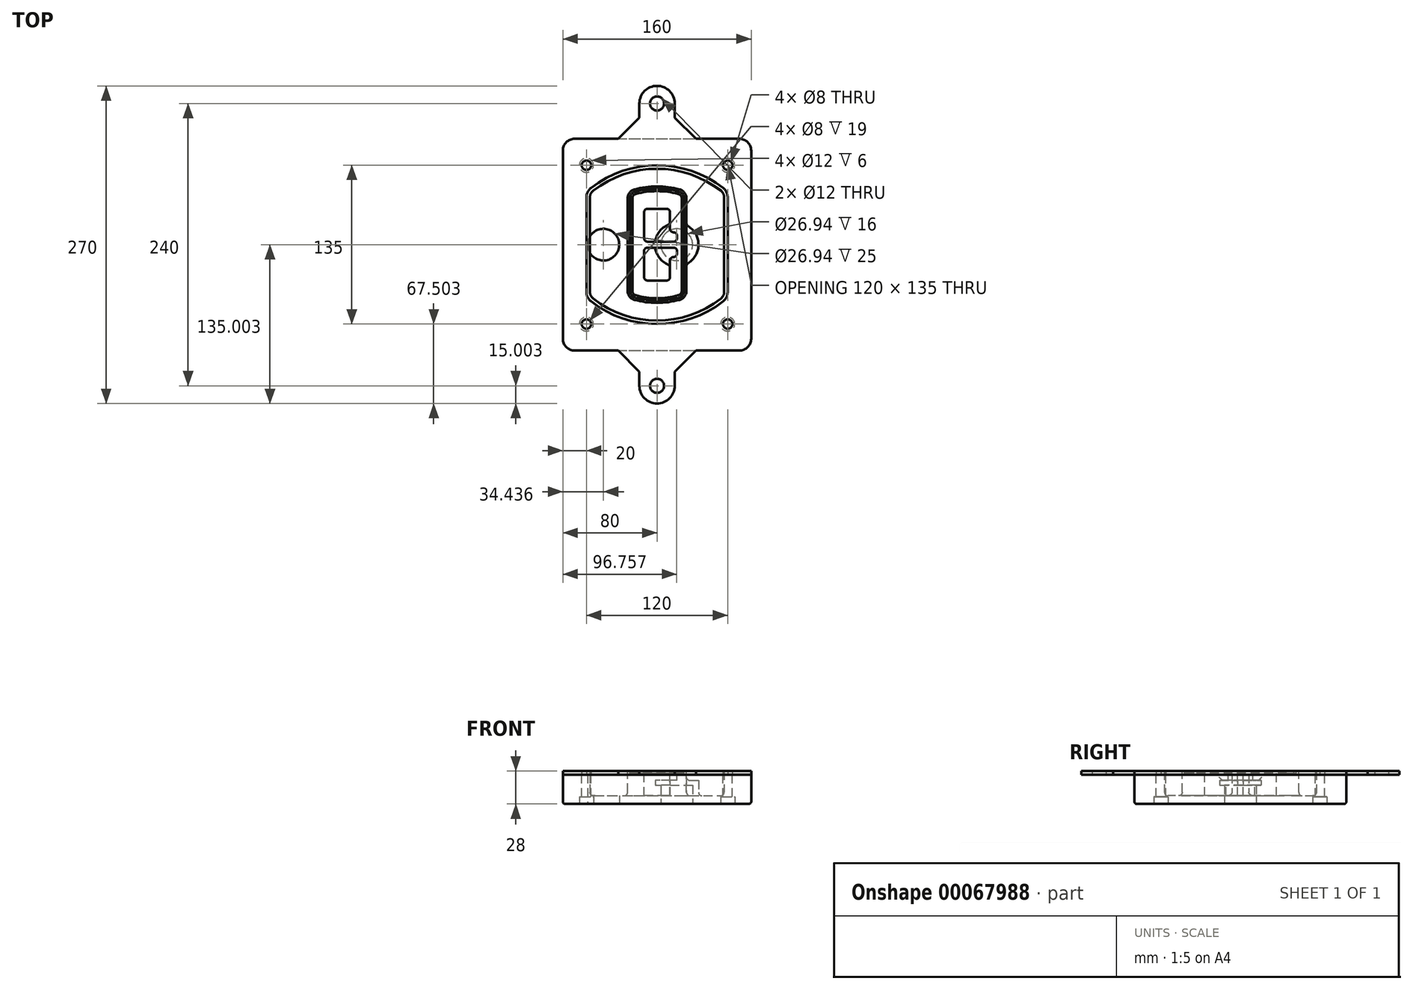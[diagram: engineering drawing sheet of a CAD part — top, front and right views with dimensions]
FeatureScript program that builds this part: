
annotation { "Feature Type Name" : "Feature", "Feature Type Description" : "" }
export const myFeature = defineFeature(function(context is Context, id is Id, definition is map)
    precondition{}
    {
        {
            var Q0;
            Q0=qCreatedBy(makeId("Top.planeOp"),FACE);
            var sketch = newSketch(context, id + "F0", { "sketchPlane" : qUnion([Q0])});
            skPoint(sketch, "E0.rect.middle", {"position": v(0, 0) * mm});
            skLineSegment(sketch, "E1.bottom", {"start": v(24.05, 28.38) * mm, "end": v(164.05, 28.38) * mm});
            skLineSegment(sketch, "E1.top", {"start": v(24.05, 208.38) * mm, "end": v(164.05, 208.38) * mm});
            skLineSegment(sketch, "E1.left", {"start": v(14.05, 38.38) * mm, "end": v(14.05, 198.38) * mm});
            skLineSegment(sketch, "E1.right", {"start": v(174.05, 38.38) * mm, "end": v(174.05, 198.38) * mm});
            skLineSegment(sketch, "E2", {"start": v(14.05, 208.38) * mm, "end": v(174.05, 28.38) * mm, "construction": true});
            skLineSegment(sketch, "E3", {"start": v(174.05, 208.38) * mm, "end": v(14.05, 28.38) * mm, "construction": true});
            skCircle(sketch, "E4", {"center": v(34.05, 185.88) * mm, "radius": 4 * mm});
            skCircle(sketch, "E5", {"center": v(154.05, 185.88) * mm, "radius": 4 * mm});
            skCircle(sketch, "E6", {"center": v(154.05, 50.88) * mm, "radius": 4 * mm});
            skCircle(sketch, "E7", {"center": v(34.05, 50.88) * mm, "radius": 4 * mm});
            skLineSegment(sketch, "E8", {"start": v(34.05, 185.88) * mm, "end": v(154.05, 185.88) * mm, "construction": true});
            skLineSegment(sketch, "E9", {"start": v(154.05, 185.88) * mm, "end": v(154.05, 50.88) * mm, "construction": true});
            skLineSegment(sketch, "E10", {"start": v(154.05, 50.88) * mm, "end": v(34.05, 50.88) * mm, "construction": true});
            skLineSegment(sketch, "E11", {"start": v(34.05, 50.88) * mm, "end": v(34.05, 185.88) * mm, "construction": true});
            skLineSegment(sketch, "E12", {"start": v(34.05, 158.68) * mm, "end": v(34.05, 78.09) * mm});
            skLineSegment(sketch, "E13", {"start": v(154.05, 158.68) * mm, "end": v(154.05, 78.09) * mm});
            skArc(sketch, "E14", {"start": v(150.2, 166.56) * mm, "mid": v(94.05, 185.88) * mm, "end": v(37.9, 166.56) * mm});
            skArc(sketch, "E15", {"start": v(37.9, 70.2) * mm, "mid": v(94.05, 50.88) * mm, "end": v(150.2, 70.2) * mm});
            skLineSegment(sketch, "E16", {"start": v(34.05, 118.38) * mm, "end": v(154.05, 118.38) * mm, "construction": true});
            skPoint(sketch, "E17.visualSharp", {"position": v(34.05, 73.38) * mm});
            skArc(sketch, "E17.filletArc", {"start": v(34.05, 78.09) * mm, "mid": v(35.06, 73.7) * mm, "end": v(37.9, 70.2) * mm});
            skPoint(sketch, "E18.visualSharp", {"position": v(34.05, 163.38) * mm});
            skArc(sketch, "E18.filletArc", {"start": v(37.9, 166.56) * mm, "mid": v(35.06, 163.06) * mm, "end": v(34.05, 158.68) * mm});
            skPoint(sketch, "E19.visualSharp", {"position": v(154.05, 163.38) * mm});
            skArc(sketch, "E19.filletArc", {"start": v(154.05, 158.68) * mm, "mid": v(153.04, 163.06) * mm, "end": v(150.2, 166.56) * mm});
            skPoint(sketch, "E20.visualSharp", {"position": v(154.05, 73.38) * mm});
            skArc(sketch, "E20.filletArc", {"start": v(150.2, 70.2) * mm, "mid": v(153.04, 73.7) * mm, "end": v(154.05, 78.09) * mm});
            skPoint(sketch, "E21.visualSharp", {"position": v(14.05, 208.38) * mm});
            skArc(sketch, "E21.filletArc", {"start": v(24.05, 208.38) * mm, "mid": v(16.98, 205.45) * mm, "end": v(14.05, 198.38) * mm});
            skPoint(sketch, "E22.visualSharp", {"position": v(174.05, 208.38) * mm});
            skArc(sketch, "E22.filletArc", {"start": v(174.05, 198.38) * mm, "mid": v(171.12, 205.45) * mm, "end": v(164.05, 208.38) * mm});
            skPoint(sketch, "E23.visualSharp", {"position": v(174.05, 28.38) * mm});
            skArc(sketch, "E23.filletArc", {"start": v(164.05, 28.38) * mm, "mid": v(171.12, 31.31) * mm, "end": v(174.05, 38.38) * mm});
            skPoint(sketch, "E24.visualSharp", {"position": v(14.05, 28.38) * mm});
            skArc(sketch, "E24.filletArc", {"start": v(14.05, 38.38) * mm, "mid": v(16.98, 31.31) * mm, "end": v(24.05, 28.38) * mm});
            skArc(sketch, "E25.0", {"start": v(151.05, 158.68) * mm, "mid": v(150.34, 161.75) * mm, "end": v(148.36, 164.2) * mm});
            skLineSegment(sketch, "E25.1", {"start": v(151.05, 158.68) * mm, "end": v(151.05, 78.09) * mm});
            skArc(sketch, "E25.2", {"start": v(148.36, 72.57) * mm, "mid": v(150.34, 75.02) * mm, "end": v(151.05, 78.09) * mm});
            skArc(sketch, "E25.3", {"start": v(39.74, 72.57) * mm, "mid": v(94.05, 53.88) * mm, "end": v(148.36, 72.57) * mm});
            skArc(sketch, "E25.4", {"start": v(37.05, 78.09) * mm, "mid": v(37.76, 75.02) * mm, "end": v(39.74, 72.57) * mm});
            skArc(sketch, "E25.5", {"start": v(148.36, 164.2) * mm, "mid": v(94.05, 182.88) * mm, "end": v(39.74, 164.2) * mm});
            skLineSegment(sketch, "E25.6", {"start": v(37.05, 158.68) * mm, "end": v(37.05, 78.09) * mm});
            skArc(sketch, "E25.7", {"start": v(39.74, 164.2) * mm, "mid": v(37.76, 161.75) * mm, "end": v(37.05, 158.68) * mm});
            skArc(sketch, "E26.0", {"start": v(35.43, 169.71) * mm, "mid": v(31.47, 164.82) * mm, "end": v(30.05, 158.68) * mm});
            skArc(sketch, "E26.1", {"start": v(152.67, 169.71) * mm, "mid": v(94.05, 189.88) * mm, "end": v(35.43, 169.71) * mm});
            skArc(sketch, "E26.2", {"start": v(158.05, 158.68) * mm, "mid": v(156.63, 164.82) * mm, "end": v(152.67, 169.71) * mm});
            skLineSegment(sketch, "E26.3", {"start": v(158.05, 158.68) * mm, "end": v(158.05, 78.09) * mm});
            skArc(sketch, "E26.4", {"start": v(152.67, 67.05) * mm, "mid": v(156.63, 71.95) * mm, "end": v(158.05, 78.09) * mm});
            skLineSegment(sketch, "E26.5", {"start": v(30.05, 158.68) * mm, "end": v(30.05, 78.09) * mm});
            skArc(sketch, "E26.6", {"start": v(35.43, 67.05) * mm, "mid": v(94.05, 46.88) * mm, "end": v(152.67, 67.05) * mm});
            skArc(sketch, "E26.7", {"start": v(30.05, 78.09) * mm, "mid": v(31.47, 71.95) * mm, "end": v(35.43, 67.05) * mm});
            skSolve(sketch);
        }
        {
            var Q0;
            Q0=makeQuery(id+"F0.imprint","IMPRINT",FACE,{"disambiguationData":[TD([[makeQuery(id+"F0.imprint","IMPRINT",EDGE,{"derivedFrom":sQuery(id+"F0.wireOp",EDGE,"E1.bottom")}),1.0]])]});
            var Q1;
            Q1=makeQuery(id+"F0.imprint","IMPRINT",FACE,{"disambiguationData":[TD([[makeQuery(id+"F0.imprint","IMPRINT",EDGE,{"derivedFrom":sQuery(id+"F0.wireOp",EDGE,"E12")}),1.0]])]});
            var Q2;
            Q2=makeQuery(id+"F0.imprint","IMPRINT",FACE,{"disambiguationData":[TD([[makeQuery(id+"F0.imprint","IMPRINT",EDGE,{"derivedFrom":sQuery(id+"F0.wireOp",EDGE,"E25.0")}),1.0]])]});
            var Q3;
            Q3=makeQuery(id+"F0.imprint","IMPRINT",FACE,{"disambiguationData":[TD([[makeQuery(id+"F0.imprint","IMPRINT",EDGE,{"derivedFrom":sQuery(id+"F0.wireOp",EDGE,"E12")}),-1.0]])]});
            extrude(context, id + "F1", {"entities" : qUnion([Q0, Q1, Q2, Q3]), "oppositeDirection" : true, "depth" : 25 * mm});
        }
        {
            var Q0;
            Q0=makeQuery(id+"F0.imprint","IMPRINT",FACE,{"disambiguationData":[TD([[makeQuery(id+"F0.imprint","IMPRINT",EDGE,{"derivedFrom":sQuery(id+"F0.wireOp",EDGE,"E12")}),1.0]])]});
            extrude(context, id + "F2", {"entities" : qUnion([Q0]), "operationType" : NewBodyOperationType.ADD, "depth" : 3 * mm});
        }
        {
            var Q0;
            Q0=makeQuery(id+"F0.imprint","IMPRINT",FACE,{"disambiguationData":[TD([[makeQuery(id+"F0.imprint","IMPRINT",EDGE,{"derivedFrom":sQuery(id+"F0.wireOp",EDGE,"E25.0")}),1.0]])]});
            extrude(context, id + "F3", {"entities" : qUnion([Q0]), "operationType" : NewBodyOperationType.REMOVE, "oppositeDirection" : true, "depth" : 18 * mm});
        }
        {
            var Q0;
            Q0=makeQuery(id+"F2.opExtrude","CAP_FACE",FACE,{"disambiguationData":[OSD([sQuery(id+"F0.wireOp",EDGE,"E12"),sQuery(id+"F0.wireOp",EDGE,"E13"),sQuery(id+"F0.wireOp",EDGE,"E14"),sQuery(id+"F0.wireOp",EDGE,"E15"),sQuery(id+"F0.wireOp",EDGE,"E17.filletArc"),sQuery(id+"F0.wireOp",EDGE,"E18.filletArc"),sQuery(id+"F0.wireOp",EDGE,"E19.filletArc"),sQuery(id+"F0.wireOp",EDGE,"E20.filletArc"),sQuery(id+"F0.wireOp",EDGE,"E25.0"),sQuery(id+"F0.wireOp",EDGE,"E25.1"),sQuery(id+"F0.wireOp",EDGE,"E25.2"),sQuery(id+"F0.wireOp",EDGE,"E25.3"),sQuery(id+"F0.wireOp",EDGE,"E25.4"),sQuery(id+"F0.wireOp",EDGE,"E25.5"),sQuery(id+"F0.wireOp",EDGE,"E25.6"),sQuery(id+"F0.wireOp",EDGE,"E25.7")])],"isStart":false});
            var sketch = newSketch(context, id + "F4", { "sketchPlane" : qUnion([Q0])});
            skArc(sketch, "E27.0", {"start": v(74.97, 71.41) * mm, "mid": v(94.05, 68.88) * mm, "end": v(113.13, 71.41) * mm});
            skArc(sketch, "E28.0", {"start": v(113.13, 165.35) * mm, "mid": v(94.05, 167.88) * mm, "end": v(74.97, 165.35) * mm});
            skLineSegment(sketch, "E29", {"start": v(69.05, 157.63) * mm, "end": v(69.05, 79.14) * mm});
            skLineSegment(sketch, "E30", {"start": v(119.05, 157.63) * mm, "end": v(119.05, 79.14) * mm});
            skLineSegment(sketch, "E31", {"start": v(69.05, 163.48) * mm, "end": v(119.05, 163.48) * mm, "construction": true});
            skLineSegment(sketch, "E32", {"start": v(69.05, 73.28) * mm, "end": v(119.05, 73.28) * mm, "construction": true});
            skPoint(sketch, "E33.visualSharp", {"position": v(69.05, 163.48) * mm});
            skArc(sketch, "E33.filletArc", {"start": v(74.97, 165.35) * mm, "mid": v(70.7, 162.5) * mm, "end": v(69.05, 157.63) * mm});
            skPoint(sketch, "E34.visualSharp", {"position": v(119.05, 163.48) * mm});
            skArc(sketch, "E34.filletArc", {"start": v(119.05, 157.63) * mm, "mid": v(117.4, 162.5) * mm, "end": v(113.13, 165.35) * mm});
            skPoint(sketch, "E35.visualSharp", {"position": v(119.05, 73.28) * mm});
            skArc(sketch, "E35.filletArc", {"start": v(113.13, 71.41) * mm, "mid": v(117.4, 74.27) * mm, "end": v(119.05, 79.14) * mm});
            skPoint(sketch, "E36.visualSharp", {"position": v(69.05, 73.28) * mm});
            skArc(sketch, "E36.filletArc", {"start": v(69.05, 79.14) * mm, "mid": v(70.7, 74.27) * mm, "end": v(74.97, 71.41) * mm});
            skArc(sketch, "E37.0", {"start": v(148.36, 164.2) * mm, "mid": v(94.05, 182.88) * mm, "end": v(39.74, 164.2) * mm});
            skArc(sketch, "E37.1", {"start": v(39.74, 164.2) * mm, "mid": v(37.76, 161.75) * mm, "end": v(37.05, 158.68) * mm});
            skLineSegment(sketch, "E37.2", {"start": v(37.05, 158.68) * mm, "end": v(37.05, 78.09) * mm});
            skArc(sketch, "E37.3", {"start": v(37.05, 78.09) * mm, "mid": v(37.76, 75.02) * mm, "end": v(39.74, 72.57) * mm});
            skArc(sketch, "E37.4", {"start": v(39.74, 72.57) * mm, "mid": v(94.05, 53.88) * mm, "end": v(148.36, 72.57) * mm});
            skArc(sketch, "E37.5", {"start": v(148.36, 72.57) * mm, "mid": v(150.34, 75.02) * mm, "end": v(151.05, 78.09) * mm});
            skLineSegment(sketch, "E37.6", {"start": v(151.05, 158.68) * mm, "end": v(151.05, 78.09) * mm});
            skArc(sketch, "E37.7", {"start": v(151.05, 158.68) * mm, "mid": v(150.34, 161.75) * mm, "end": v(148.36, 164.2) * mm});
            skLineSegment(sketch, "E38.0", {"start": v(117.05, 157.63) * mm, "end": v(117.05, 79.14) * mm});
            skArc(sketch, "E38.1", {"start": v(112.61, 73.34) * mm, "mid": v(115.81, 75.49) * mm, "end": v(117.05, 79.14) * mm});
            skArc(sketch, "E38.2", {"start": v(75.49, 73.34) * mm, "mid": v(94.05, 70.88) * mm, "end": v(112.61, 73.34) * mm});
            skArc(sketch, "E38.3", {"start": v(71.05, 79.14) * mm, "mid": v(72.29, 75.49) * mm, "end": v(75.49, 73.34) * mm});
            skLineSegment(sketch, "E38.4", {"start": v(71.05, 157.63) * mm, "end": v(71.05, 79.14) * mm});
            skArc(sketch, "E38.5", {"start": v(117.05, 157.63) * mm, "mid": v(115.81, 161.28) * mm, "end": v(112.61, 163.42) * mm});
            skArc(sketch, "E38.6", {"start": v(75.49, 163.42) * mm, "mid": v(72.29, 161.28) * mm, "end": v(71.05, 157.63) * mm});
            skArc(sketch, "E38.7", {"start": v(112.61, 163.42) * mm, "mid": v(94.05, 165.88) * mm, "end": v(75.49, 163.42) * mm});
            skArc(sketch, "E39.0", {"start": v(115.05, 157.63) * mm, "mid": v(114.23, 160.06) * mm, "end": v(112.1, 161.5) * mm});
            skLineSegment(sketch, "E39.1", {"start": v(115.05, 157.63) * mm, "end": v(115.05, 79.14) * mm});
            skArc(sketch, "E39.2", {"start": v(112.1, 75.27) * mm, "mid": v(114.23, 76.7) * mm, "end": v(115.05, 79.14) * mm});
            skArc(sketch, "E39.3", {"start": v(76, 75.27) * mm, "mid": v(94.05, 72.88) * mm, "end": v(112.1, 75.27) * mm});
            skArc(sketch, "E39.4", {"start": v(73.05, 79.14) * mm, "mid": v(73.87, 76.7) * mm, "end": v(76, 75.27) * mm});
            skArc(sketch, "E39.5", {"start": v(112.1, 161.5) * mm, "mid": v(94.05, 163.88) * mm, "end": v(76, 161.5) * mm});
            skLineSegment(sketch, "E39.6", {"start": v(73.05, 157.63) * mm, "end": v(73.05, 79.14) * mm});
            skArc(sketch, "E39.7", {"start": v(76, 161.5) * mm, "mid": v(73.87, 160.06) * mm, "end": v(73.05, 157.63) * mm});
            skLineSegment(sketch, "E40", {"start": v(69.05, 118.38) * mm, "end": v(119.05, 118.38) * mm, "construction": true});
            skLineSegment(sketch, "E41", {"start": v(83.05, 123.88) * mm, "end": v(83.05, 145.88) * mm});
            skLineSegment(sketch, "E42", {"start": v(86.05, 148.88) * mm, "end": v(102.05, 148.88) * mm});
            skLineSegment(sketch, "E43", {"start": v(105.05, 145.88) * mm, "end": v(105.05, 131.88) * mm});
            skLineSegment(sketch, "E44", {"start": v(108.05, 128.88) * mm, "end": v(108.05, 128.88) * mm});
            skLineSegment(sketch, "E45", {"start": v(111.05, 125.88) * mm, "end": v(111.05, 123.88) * mm});
            skLineSegment(sketch, "E46", {"start": v(108.05, 120.88) * mm, "end": v(86.05, 120.88) * mm});
            skPoint(sketch, "E47.visualSharp", {"position": v(83.05, 148.88) * mm});
            skArc(sketch, "E47.filletArc", {"start": v(86.05, 148.88) * mm, "mid": v(83.93, 148) * mm, "end": v(83.05, 145.88) * mm});
            skPoint(sketch, "E48.visualSharp", {"position": v(105.05, 148.88) * mm});
            skArc(sketch, "E48.filletArc", {"start": v(105.05, 145.88) * mm, "mid": v(104.17, 148) * mm, "end": v(102.05, 148.88) * mm});
            skPoint(sketch, "E49.visualSharp", {"position": v(105.05, 128.88) * mm});
            skArc(sketch, "E49.filletArc", {"start": v(105.05, 131.88) * mm, "mid": v(105.93, 129.76) * mm, "end": v(108.05, 128.88) * mm});
            skPoint(sketch, "E50.visualSharp", {"position": v(111.05, 128.88) * mm});
            skArc(sketch, "E50.filletArc", {"start": v(111.05, 125.88) * mm, "mid": v(110.17, 128) * mm, "end": v(108.05, 128.88) * mm});
            skPoint(sketch, "E51.visualSharp", {"position": v(111.05, 120.88) * mm});
            skArc(sketch, "E51.filletArc", {"start": v(108.05, 120.88) * mm, "mid": v(110.17, 121.76) * mm, "end": v(111.05, 123.88) * mm});
            skPoint(sketch, "E52.visualSharp", {"position": v(83.05, 120.88) * mm});
            skArc(sketch, "E52.filletArc", {"start": v(83.05, 123.88) * mm, "mid": v(83.93, 121.76) * mm, "end": v(86.05, 120.88) * mm});
            skLineSegment(sketch, "E53.0.MirrorCS", {"start": v(108.05, 115.88) * mm, "end": v(86.05, 115.88) * mm});
            skArc(sketch, "E54.0.MirrorCS", {"start": v(83.05, 112.88) * mm, "mid": v(83.93, 115) * mm, "end": v(86.05, 115.88) * mm});
            skLineSegment(sketch, "E55.0.MirrorCS", {"start": v(83.05, 112.88) * mm, "end": v(83.05, 90.88) * mm});
            skArc(sketch, "E56.0.MirrorCS", {"start": v(86.05, 87.88) * mm, "mid": v(83.93, 88.76) * mm, "end": v(83.05, 90.88) * mm});
            skLineSegment(sketch, "E57.0.MirrorCS", {"start": v(86.05, 87.88) * mm, "end": v(102.05, 87.88) * mm});
            skArc(sketch, "E58.0.MirrorCS", {"start": v(105.05, 90.88) * mm, "mid": v(104.17, 88.76) * mm, "end": v(102.05, 87.88) * mm});
            skLineSegment(sketch, "E59.0.MirrorCS", {"start": v(105.05, 90.88) * mm, "end": v(105.05, 104.88) * mm});
            skArc(sketch, "E60.0.MirrorCS", {"start": v(105.05, 104.88) * mm, "mid": v(105.93, 107) * mm, "end": v(108.05, 107.88) * mm});
            skArc(sketch, "E61.0.MirrorCS", {"start": v(111.05, 110.88) * mm, "mid": v(110.17, 108.76) * mm, "end": v(108.05, 107.88) * mm});
            skLineSegment(sketch, "E62.0.MirrorCS", {"start": v(111.05, 110.88) * mm, "end": v(111.05, 112.88) * mm});
            skArc(sketch, "E63.0.MirrorCS", {"start": v(108.05, 115.88) * mm, "mid": v(110.17, 115) * mm, "end": v(111.05, 112.88) * mm});
            skSolve(sketch);
        }
        {
            var Q0;
            Q0=makeQuery(id+"F4.imprint","IMPRINT",FACE,{"disambiguationData":[TD([[makeQuery(id+"F4.imprint","IMPRINT",EDGE,{"derivedFrom":sQuery(id+"F4.wireOp",EDGE,"E27.0")}),1.0]])]});
            var Q1;
            Q1=makeQuery(id+"F4.imprint","IMPRINT",FACE,{"disambiguationData":[TD([[makeQuery(id+"F4.imprint","IMPRINT",EDGE,{"derivedFrom":sQuery(id+"F4.wireOp",EDGE,"E38.0")}),-1.0]])]});
            var Q2;
            Q2=makeQuery(id+"F4.imprint","IMPRINT",FACE,{"disambiguationData":[TD([[makeQuery(id+"F4.imprint","IMPRINT",EDGE,{"derivedFrom":sQuery(id+"F4.wireOp",EDGE,"E39.0")}),1.0]])]});
            extrude(context, id + "F5", {"entities" : qUnion([Q0, Q1, Q2]), "operationType" : NewBodyOperationType.ADD, "endBound" : BoundingType.UP_TO_NEXT, "oppositeDirection" : true, "depth" : 25 * mm});
        }
        {
            var Q0;
            Q0=makeQuery(id+"F4.imprint","IMPRINT",FACE,{"disambiguationData":[TD([[makeQuery(id+"F4.imprint","IMPRINT",EDGE,{"derivedFrom":sQuery(id+"F4.wireOp",EDGE,"E38.0")}),-1.0]])]});
            extrude(context, id + "F6", {"entities" : qUnion([Q0]), "operationType" : NewBodyOperationType.REMOVE, "oppositeDirection" : true, "depth" : 2 * mm});
        }
        {
            var Q0;
            Q0=makeQuery(id+"F1.opExtrude","CAP_FACE",FACE,{"disambiguationData":[OSD([sQuery(id+"F0.wireOp",EDGE,"E1.bottom"),sQuery(id+"F0.wireOp",EDGE,"E1.top"),sQuery(id+"F0.wireOp",EDGE,"E1.left"),sQuery(id+"F0.wireOp",EDGE,"E1.right"),sQuery(id+"F0.wireOp",EDGE,"E4"),sQuery(id+"F0.wireOp",EDGE,"E5"),sQuery(id+"F0.wireOp",EDGE,"E6"),sQuery(id+"F0.wireOp",EDGE,"E7"),sQuery(id+"F0.wireOp",EDGE,"E21.filletArc"),sQuery(id+"F0.wireOp",EDGE,"E22.filletArc"),sQuery(id+"F0.wireOp",EDGE,"E23.filletArc"),sQuery(id+"F0.wireOp",EDGE,"E24.filletArc")])],"isStart":false});
            var sketch = newSketch(context, id + "F7", { "sketchPlane" : qUnion([Q0])});
            skCircle(sketch, "E64", {"center": v(110.8, -118.38) * mm, "radius": 13.47 * mm});
            skCircle(sketch, "E65", {"center": v(48.49, -118.38) * mm, "radius": 13.47 * mm});
            skLineSegment(sketch, "E66", {"start": v(174.05, -118.38) * mm, "end": v(14.05, -118.38) * mm});
            skCircle(sketch, "E67", {"center": v(110.8, -118.38) * mm, "radius": 18.47 * mm});
            skCircle(sketch, "E68", {"center": v(154.05, -185.88) * mm, "radius": 6 * mm});
            skCircle(sketch, "E69", {"center": v(34.05, -185.88) * mm, "radius": 6 * mm});
            skCircle(sketch, "E70", {"center": v(34.05, -50.88) * mm, "radius": 6 * mm});
            skCircle(sketch, "E71", {"center": v(154.05, -50.88) * mm, "radius": 6 * mm});
            skSolve(sketch);
        }
        {
            var Q0;
            {var subQ1=sQuery(id+"F7.wireOp",EDGE,"E66");var subQ4=sQuery(id+"F7.wireOp",EDGE,"E64");var subQ6=makeQuery(id+"F7.imprint","INTERSECT",VERTEX,{"disambiguationData":[OD(0.0)],"derivedFrom":[subQ4,subQ1]});Q0=makeQuery(id+"F7.imprint","IMPRINT",FACE,{"disambiguationData":[TD([[makeQuery(id+"F7.imprint","IMPRINT",EDGE,{"disambiguationData":[TD([[subQ6,-1.0]])],"derivedFrom":subQ4}),-1.0]])]});}
            var Q1;
            {var subQ0=sQuery(id+"F7.wireOp",EDGE,"E66");var subQ1=sQuery(id+"F7.wireOp",EDGE,"E64");var subQ3=makeQuery(id+"F7.imprint","INTERSECT",VERTEX,{"disambiguationData":[OD(0.0)],"derivedFrom":[subQ1,subQ0]});Q1=makeQuery(id+"F7.imprint","IMPRINT",FACE,{"disambiguationData":[TD([[makeQuery(id+"F7.imprint","IMPRINT",EDGE,{"disambiguationData":[TD([[subQ3,-1.0]])],"derivedFrom":subQ1}),1.0]])]});}
            var Q2;
            {var subQ0=sQuery(id+"F7.wireOp",EDGE,"E66");var subQ1=sQuery(id+"F7.wireOp",EDGE,"E64");var subQ3=makeQuery(id+"F7.imprint","INTERSECT",VERTEX,{"disambiguationData":[OD(0.0)],"derivedFrom":[subQ1,subQ0]});Q2=makeQuery(id+"F7.imprint","IMPRINT",FACE,{"disambiguationData":[TD([[makeQuery(id+"F7.imprint","IMPRINT",EDGE,{"disambiguationData":[TD([[subQ3,1.0]])],"derivedFrom":subQ1}),1.0]])]});}
            var Q3;
            {var subQ1=sQuery(id+"F7.wireOp",EDGE,"E66");var subQ4=sQuery(id+"F7.wireOp",EDGE,"E64");var subQ6=makeQuery(id+"F7.imprint","INTERSECT",VERTEX,{"disambiguationData":[OD(0.0)],"derivedFrom":[subQ4,subQ1]});Q3=makeQuery(id+"F7.imprint","IMPRINT",FACE,{"disambiguationData":[TD([[makeQuery(id+"F7.imprint","IMPRINT",EDGE,{"disambiguationData":[TD([[subQ6,1.0]])],"derivedFrom":subQ4}),-1.0]])]});}
            extrude(context, id + "F8", {"entities" : qUnion([Q0, Q1, Q2, Q3]), "operationType" : NewBodyOperationType.ADD, "oppositeDirection" : true, "depth" : 20 * mm});
        }
        {
            var Q0;
            {var subQ0=sQuery(id+"F7.wireOp",EDGE,"E66");var subQ1=sQuery(id+"F7.wireOp",EDGE,"E64");var subQ3=makeQuery(id+"F7.imprint","INTERSECT",VERTEX,{"disambiguationData":[OD(0.0)],"derivedFrom":[subQ1,subQ0]});Q0=makeQuery(id+"F7.imprint","IMPRINT",FACE,{"disambiguationData":[TD([[makeQuery(id+"F7.imprint","IMPRINT",EDGE,{"disambiguationData":[TD([[subQ3,-1.0]])],"derivedFrom":subQ1}),1.0]])]});}
            var Q1;
            {var subQ0=sQuery(id+"F7.wireOp",EDGE,"E66");var subQ1=sQuery(id+"F7.wireOp",EDGE,"E64");var subQ3=makeQuery(id+"F7.imprint","INTERSECT",VERTEX,{"disambiguationData":[OD(0.0)],"derivedFrom":[subQ1,subQ0]});Q1=makeQuery(id+"F7.imprint","IMPRINT",FACE,{"disambiguationData":[TD([[makeQuery(id+"F7.imprint","IMPRINT",EDGE,{"disambiguationData":[TD([[subQ3,1.0]])],"derivedFrom":subQ1}),1.0]])]});}
            extrude(context, id + "F9", {"entities" : qUnion([Q0, Q1]), "operationType" : NewBodyOperationType.REMOVE, "oppositeDirection" : true, "depth" : 16 * mm});
        }
        {
            var Q0;
            {var subQ0=sQuery(id+"F7.wireOp",EDGE,"E66");var subQ1=sQuery(id+"F7.wireOp",EDGE,"E65");var subQ3=makeQuery(id+"F7.imprint","INTERSECT",VERTEX,{"disambiguationData":[OD(0.0)],"derivedFrom":[subQ1,subQ0]});Q0=makeQuery(id+"F7.imprint","IMPRINT",FACE,{"disambiguationData":[TD([[makeQuery(id+"F7.imprint","IMPRINT",EDGE,{"disambiguationData":[TD([[subQ3,-1.0]])],"derivedFrom":subQ1}),1.0]])]});}
            var Q1;
            {var subQ0=sQuery(id+"F7.wireOp",EDGE,"E66");var subQ1=sQuery(id+"F7.wireOp",EDGE,"E65");var subQ3=makeQuery(id+"F7.imprint","INTERSECT",VERTEX,{"disambiguationData":[OD(0.0)],"derivedFrom":[subQ1,subQ0]});Q1=makeQuery(id+"F7.imprint","IMPRINT",FACE,{"disambiguationData":[TD([[makeQuery(id+"F7.imprint","IMPRINT",EDGE,{"disambiguationData":[TD([[subQ3,1.0]])],"derivedFrom":subQ1}),1.0]])]});}
            extrude(context, id + "F10", {"entities" : qUnion([Q0, Q1]), "operationType" : NewBodyOperationType.REMOVE, "oppositeDirection" : true, "depth" : 25 * mm});
        }
        {
            var Q0;
            Q0=makeQuery(id+"F7.imprint","IMPRINT",FACE,{"disambiguationData":[TD([[makeQuery(id+"F7.imprint","IMPRINT",EDGE,{"derivedFrom":sQuery(id+"F7.wireOp",EDGE,"E68")}),1.0]])]});
            var Q1;
            Q1=makeQuery(id+"F7.imprint","IMPRINT",FACE,{"disambiguationData":[TD([[makeQuery(id+"F7.imprint","IMPRINT",EDGE,{"derivedFrom":makeQuery(id+"F1.opExtrude","CAP_EDGE",EDGE,{"disambiguationData":[OSD([sQuery(id+"F0.wireOp",EDGE,"E5")])],"isStart":false})}),-1.0]])]});
            var Q2;
            Q2=makeQuery(id+"F7.imprint","IMPRINT",FACE,{"disambiguationData":[TD([[makeQuery(id+"F7.imprint","IMPRINT",EDGE,{"derivedFrom":sQuery(id+"F7.wireOp",EDGE,"E69")}),1.0]])]});
            var Q3;
            Q3=makeQuery(id+"F7.imprint","IMPRINT",FACE,{"disambiguationData":[TD([[makeQuery(id+"F7.imprint","IMPRINT",EDGE,{"derivedFrom":makeQuery(id+"F1.opExtrude","CAP_EDGE",EDGE,{"disambiguationData":[OSD([sQuery(id+"F0.wireOp",EDGE,"E4")])],"isStart":false})}),-1.0]])]});
            var Q4;
            Q4=makeQuery(id+"F7.imprint","IMPRINT",FACE,{"disambiguationData":[TD([[makeQuery(id+"F7.imprint","IMPRINT",EDGE,{"derivedFrom":sQuery(id+"F7.wireOp",EDGE,"E70")}),1.0]])]});
            var Q5;
            Q5=makeQuery(id+"F7.imprint","IMPRINT",FACE,{"disambiguationData":[TD([[makeQuery(id+"F7.imprint","IMPRINT",EDGE,{"derivedFrom":makeQuery(id+"F1.opExtrude","CAP_EDGE",EDGE,{"disambiguationData":[OSD([sQuery(id+"F0.wireOp",EDGE,"E7")])],"isStart":false})}),-1.0]])]});
            var Q6;
            Q6=makeQuery(id+"F7.imprint","IMPRINT",FACE,{"disambiguationData":[TD([[makeQuery(id+"F7.imprint","IMPRINT",EDGE,{"derivedFrom":sQuery(id+"F7.wireOp",EDGE,"E71")}),1.0]])]});
            var Q7;
            Q7=makeQuery(id+"F7.imprint","IMPRINT",FACE,{"disambiguationData":[TD([[makeQuery(id+"F7.imprint","IMPRINT",EDGE,{"derivedFrom":makeQuery(id+"F1.opExtrude","CAP_EDGE",EDGE,{"disambiguationData":[OSD([sQuery(id+"F0.wireOp",EDGE,"E6")])],"isStart":false})}),-1.0]])]});
            extrude(context, id + "F11", {"entities" : qUnion([Q0, Q1, Q2, Q3, Q4, Q5, Q6, Q7]), "operationType" : NewBodyOperationType.REMOVE, "oppositeDirection" : true, "depth" : 6 * mm});
        }
        {
            var Q0;
            Q0=makeQuery(id+"F9.boolean.opBoolean","COPY",FACE,{"derivedFrom":makeQuery(id+"F9.opExtrude","CAP_FACE",FACE,{"disambiguationData":[OSD([sQuery(id+"F7.wireOp",EDGE,"E64")])],"isStart":false})});
            var sketch = newSketch(context, id + "F12", { "sketchPlane" : qUnion([Q0])});
            skArc(sketch, "E72.0", {"start": v(105.05, -100.83) * mm, "mid": v(96.62, -106.56) * mm, "end": v(92.5, -115.88) * mm});
            skArc(sketch, "E72.1", {"start": v(92.5, -120.88) * mm, "mid": v(96.62, -130.2) * mm, "end": v(105.05, -135.93) * mm});
            skLineSegment(sketch, "E73", {"start": v(92.5, -120.88) * mm, "end": v(108.05, -120.88) * mm});
            skLineSegment(sketch, "E74.0", {"start": v(108.05, -115.88) * mm, "end": v(92.5, -115.88) * mm});
            skArc(sketch, "E74.1", {"start": v(108.05, -115.88) * mm, "mid": v(110.17, -115) * mm, "end": v(111.05, -112.88) * mm});
            skLineSegment(sketch, "E74.2", {"start": v(111.05, -110.88) * mm, "end": v(111.05, -112.88) * mm});
            skArc(sketch, "E74.3", {"start": v(111.05, -110.88) * mm, "mid": v(110.17, -108.76) * mm, "end": v(108.05, -107.88) * mm});
            skArc(sketch, "E74.4", {"start": v(105.05, -104.88) * mm, "mid": v(105.93, -107) * mm, "end": v(108.05, -107.88) * mm});
            skLineSegment(sketch, "E74.5", {"start": v(105.05, -100.83) * mm, "end": v(105.05, -104.88) * mm});
            skLineSegment(sketch, "E74.7", {"start": v(108.05, -120.88) * mm, "end": v(92.5, -120.88) * mm});
            skArc(sketch, "E74.8", {"start": v(108.05, -120.88) * mm, "mid": v(110.17, -121.76) * mm, "end": v(111.05, -123.88) * mm});
            skLineSegment(sketch, "E74.9", {"start": v(111.05, -125.88) * mm, "end": v(111.05, -123.88) * mm});
            skArc(sketch, "E74.10", {"start": v(111.05, -125.88) * mm, "mid": v(110.17, -128) * mm, "end": v(108.05, -128.88) * mm});
            skArc(sketch, "E74.11", {"start": v(105.05, -131.88) * mm, "mid": v(105.93, -129.76) * mm, "end": v(108.05, -128.88) * mm});
            skLineSegment(sketch, "E74.12", {"start": v(105.05, -135.93) * mm, "end": v(105.05, -131.88) * mm});
            skPoint(sketch, "E75.orphan", {"position": v(105.05, -145.88) * mm});
            skPoint(sketch, "E76.orphan", {"position": v(86.05, -120.88) * mm});
            skPoint(sketch, "E77.orphan", {"position": v(86.05, -115.88) * mm});
            skPoint(sketch, "E78.orphan", {"position": v(105.05, -90.88) * mm});
            skSolve(sketch);
        }
        {
            var Q0;
            {var subQ7=sQuery(id+"F12.wireOp",EDGE,"E72.0");var subQ14=sQuery(id+"F12.wireOp",EDGE,"E72.1");var subQ16=sQuery(id+"F12.wireOp",EDGE,"E74.1");var subQ18=sQuery(id+"F12.wireOp",EDGE,"E74.8");Q0=qUnion([makeQuery(id+"F12.imprint","IMPRINT",FACE,{"disambiguationData":[TD([[makeQuery(id+"F12.imprint","IMPRINT",EDGE,{"derivedFrom":subQ7}),1.0]])]}),makeQuery(id+"F12.imprint","IMPRINT",FACE,{"disambiguationData":[TD([[makeQuery(id+"F12.imprint","IMPRINT",EDGE,{"derivedFrom":subQ14}),1.0]])]}),makeQuery(id+"F12.imprint","IMPRINT",FACE,{"disambiguationData":[TD([[makeQuery(id+"F12.imprint","IMPRINT",EDGE,{"derivedFrom":subQ16}),1.0]])]}),makeQuery(id+"F12.imprint","IMPRINT",FACE,{"disambiguationData":[TD([[makeQuery(id+"F12.imprint","IMPRINT",EDGE,{"derivedFrom":subQ18}),-1.0]])]})]);}
            var Q1;
            Q1=makeQuery(id+"F5.boolean.opBoolean","SPLIT",FACE,{"disambiguationData":[TD([makeQuery(id+"F5.opExtrude","SWEPT_FACE",FACE,{"disambiguationData":[OSD([sQuery(id+"F4.wireOp",EDGE,"E41")])]})])],"derivedFrom":makeQuery(id+"F3.boolean.opBoolean","COPY",FACE,{"derivedFrom":makeQuery(id+"F3.opExtrude","CAP_FACE",FACE,{"disambiguationData":[OSD([sQuery(id+"F0.wireOp",EDGE,"E25.0"),sQuery(id+"F0.wireOp",EDGE,"E25.1"),sQuery(id+"F0.wireOp",EDGE,"E25.2"),sQuery(id+"F0.wireOp",EDGE,"E25.3"),sQuery(id+"F0.wireOp",EDGE,"E25.4"),sQuery(id+"F0.wireOp",EDGE,"E25.5"),sQuery(id+"F0.wireOp",EDGE,"E25.6"),sQuery(id+"F0.wireOp",EDGE,"E25.7")])],"isStart":false})})});
            extrude(context, id + "F13", {"entities" : qUnion([Q0]), "operationType" : NewBodyOperationType.REMOVE, "endBound" : BoundingType.UP_TO_SURFACE, "endBoundEntityFace" : qUnion([Q1]), "depth" : 25 * mm});
        }
        {
            var Q0;
            Q0=makeQuery(id+"F3.boolean.opBoolean","COPY",EDGE,{"derivedFrom":makeQuery(id+"F3.opExtrude","CAP_EDGE",EDGE,{"disambiguationData":[OSD([sQuery(id+"F0.wireOp",EDGE,"E25.6")])],"isStart":false})});
            var Q1;
            Q1=makeQuery(id+"F8.boolean.opBoolean","INTERSECT",EDGE,{"derivedFrom":[makeQuery(id+"F5.opExtrude","SWEPT_FACE",FACE,{"disambiguationData":[OSD([sQuery(id+"F4.wireOp",EDGE,"E30")])]}),makeQuery(id+"F8.opExtrude","CAP_FACE",FACE,{"disambiguationData":[OSD([sQuery(id+"F7.wireOp",EDGE,"E67")])],"isStart":false})]});
            var Q2;
            Q2=makeQuery(id+"F8.boolean.opBoolean","INTERSECT",EDGE,{"disambiguationData":[OD(1.0)],"derivedFrom":[makeQuery(id+"F5.opExtrude","SWEPT_FACE",FACE,{"disambiguationData":[OSD([sQuery(id+"F4.wireOp",EDGE,"E30")])]}),makeQuery(id+"F8.opExtrude","SWEPT_FACE",FACE,{"disambiguationData":[OSD([sQuery(id+"F7.wireOp",EDGE,"E67")])]})]});
            var Q3;
            {var subQ0=sQuery(id+"F4.wireOp",EDGE,"E30");Q3=makeQuery(id+"F8.boolean.opBoolean","SPLIT",EDGE,{"disambiguationData":[TD([makeQuery(id+"F5.opExtrude","SWEPT_FACE",FACE,{"disambiguationData":[OSD([sQuery(id+"F4.wireOp",EDGE,"E35.filletArc")])]})])],"derivedFrom":makeQuery(id+"F5.opExtrude","CAP_EDGE",EDGE,{"disambiguationData":[OSD([subQ0])],"isStart":false})});}
            var Q4;
            {var subQ0=sQuery(id+"F0.wireOp",EDGE,"E25.7");var subQ1=sQuery(id+"F0.wireOp",EDGE,"E25.1");var subQ2=sQuery(id+"F0.wireOp",EDGE,"E25.6");var subQ3=sQuery(id+"F0.wireOp",EDGE,"E25.5");var subQ4=sQuery(id+"F0.wireOp",EDGE,"E25.4");var subQ5=sQuery(id+"F0.wireOp",EDGE,"E25.0");var subQ6=sQuery(id+"F0.wireOp",EDGE,"E25.2");var subQ7=sQuery(id+"F0.wireOp",EDGE,"E25.3");Q4=makeQuery(id+"F8.boolean.opBoolean","INTERSECT",EDGE,{"derivedFrom":[makeQuery(id+"F5.boolean.opBoolean","SPLIT",FACE,{"disambiguationData":[TD([makeQuery(id+"F2.opExtrude","SWEPT_FACE",FACE,{"disambiguationData":[OSD([subQ5])]})])],"derivedFrom":makeQuery(id+"F3.boolean.opBoolean","COPY",FACE,{"derivedFrom":makeQuery(id+"F3.opExtrude","CAP_FACE",FACE,{"disambiguationData":[OSD([subQ5,subQ1,subQ6,subQ7,subQ4,subQ3,subQ2,subQ0])],"isStart":false})})}),makeQuery(id+"F8.opExtrude","SWEPT_FACE",FACE,{"disambiguationData":[OSD([sQuery(id+"F7.wireOp",EDGE,"E67")])]})]});}
            var Q5;
            Q5=makeQuery(id+"F8.boolean.opBoolean","INTERSECT",EDGE,{"disambiguationData":[OD(0.0)],"derivedFrom":[makeQuery(id+"F5.opExtrude","SWEPT_FACE",FACE,{"disambiguationData":[OSD([sQuery(id+"F4.wireOp",EDGE,"E30")])]}),makeQuery(id+"F8.opExtrude","SWEPT_FACE",FACE,{"disambiguationData":[OSD([sQuery(id+"F7.wireOp",EDGE,"E67")])]})]});
            fillet(context, id + "F14", {"entities" : qUnion([Q0, Q1, Q2, Q3, Q4, Q5]), "radius" : 3 * mm, "tangentPropagation" : true, "allowEdgeOverflow" : false});
        }
        {
            var Q0;
            Q0=makeQuery(id+"F1.opExtrude","CAP_EDGE",EDGE,{"disambiguationData":[OSD([sQuery(id+"F0.wireOp",EDGE,"E1.bottom")])],"isStart":false});
            fillet(context, id + "F15", {"entities" : qUnion([Q0]), "radius" : 2 * mm, "tangentPropagation" : true, "allowEdgeOverflow" : false});
        }
        {
            var Q0;
            {var subQ0=sQuery(id+"F0.wireOp",EDGE,"E22.filletArc");var subQ1=sQuery(id+"F0.wireOp",EDGE,"E7");var subQ2=sQuery(id+"F0.wireOp",EDGE,"E6");var subQ3=sQuery(id+"F0.wireOp",EDGE,"E5");var subQ4=sQuery(id+"F0.wireOp",EDGE,"E4");var subQ5=sQuery(id+"F0.wireOp",EDGE,"E1.bottom");var subQ6=sQuery(id+"F0.wireOp",EDGE,"E21.filletArc");var subQ7=sQuery(id+"F0.wireOp",EDGE,"E1.top");var subQ8=sQuery(id+"F0.wireOp",EDGE,"E1.left");var subQ9=sQuery(id+"F0.wireOp",EDGE,"E1.right");var subQ10=sQuery(id+"F0.wireOp",EDGE,"E23.filletArc");var subQ11=sQuery(id+"F0.wireOp",EDGE,"E24.filletArc");Q0=makeQuery(id+"F2.boolean.opBoolean","SPLIT",FACE,{"disambiguationData":[TD([makeQuery(id+"F1.opExtrude","SWEPT_FACE",FACE,{"disambiguationData":[OSD([subQ5])]})])],"derivedFrom":makeQuery(id+"F1.opExtrude","CAP_FACE",FACE,{"disambiguationData":[OSD([subQ5,subQ7,subQ8,subQ9,subQ4,subQ3,subQ2,subQ1,subQ6,subQ0,subQ10,subQ11])],"isStart":true})});}
            var sketch = newSketch(context, id + "F16", { "sketchPlane" : qUnion([Q0])});
            skLineSegment(sketch, "E79", {"start": v(94.05, 28.38) * mm, "end": v(94.05, 208.38) * mm, "construction": true});
            skLineSegment(sketch, "E80", {"start": v(94.05, 118.38) * mm, "end": v(14.05, 118.38) * mm, "construction": true});
            skLineSegment(sketch, "E81", {"start": v(94.05, 208.38) * mm, "end": v(94.05, 238.38) * mm, "construction": true});
            skCircle(sketch, "E82", {"center": v(94.05, 238.38) * mm, "radius": 6 * mm});
            skArc(sketch, "E83", {"start": v(109.05, 238.38) * mm, "mid": v(94.05, 253.38) * mm, "end": v(79.05, 238.38) * mm});
            skLineSegment(sketch, "E84", {"start": v(109.05, 238.38) * mm, "end": v(109.05, 226.38) * mm});
            skLineSegment(sketch, "E85", {"start": v(109.05, 226.38) * mm, "end": v(127.05, 208.38) * mm});
            skLineSegment(sketch, "E86.MirrorCS", {"start": v(79.05, 238.38) * mm, "end": v(79.05, 226.38) * mm});
            skLineSegment(sketch, "E87.MirrorCS", {"start": v(79.05, 226.38) * mm, "end": v(61.05, 208.38) * mm});
            skLineSegment(sketch, "E88.MirrorCS", {"start": v(79.05, 10.38) * mm, "end": v(61.05, 28.38) * mm});
            skLineSegment(sketch, "E89.MirrorCS", {"start": v(79.05, -1.62) * mm, "end": v(79.05, 10.38) * mm});
            skArc(sketch, "E90.MirrorCS", {"start": v(109.05, -1.62) * mm, "mid": v(94.05, -16.62) * mm, "end": v(79.05, -1.62) * mm});
            skCircle(sketch, "E91.MirrorC", {"center": v(94.05, -1.62) * mm, "radius": 6 * mm});
            skLineSegment(sketch, "E92.MirrorCS", {"start": v(109.05, -1.62) * mm, "end": v(109.05, 10.38) * mm});
            skLineSegment(sketch, "E93.MirrorCS", {"start": v(109.05, 10.38) * mm, "end": v(127.05, 28.38) * mm});
            skSolve(sketch);
        }
        {
            var Q0;
            Q0=makeQuery(id+"F16.imprint","IMPRINT",FACE,{"disambiguationData":[TD([[makeQuery(id+"F16.imprint","IMPRINT",EDGE,{"derivedFrom":sQuery(id+"F16.wireOp",EDGE,"E82")}),-1.0]])]});
            var Q1;
            Q1=makeQuery(id+"F16.imprint","IMPRINT",FACE,{"disambiguationData":[TD([[makeQuery(id+"F16.imprint","IMPRINT",EDGE,{"derivedFrom":makeQuery(id+"F1.opExtrude","CAP_EDGE",EDGE,{"disambiguationData":[OSD([sQuery(id+"F0.wireOp",EDGE,"E1.left")])],"isStart":true})}),-1.0]])]});
            var Q2;
            {var subQ0=sQuery(id+"F16.wireOp",EDGE,"E88.MirrorCS");Q2=makeQuery(id+"F16.imprint","IMPRINT",FACE,{"disambiguationData":[TD([[makeQuery(id+"F16.imprint","IMPRINT",EDGE,{"derivedFrom":subQ0}),-1.0]])]});}
            var Q3;
            Q3=makeQuery(id+"F2.opExtrude","CAP_FACE",FACE,{"disambiguationData":[OSD([sQuery(id+"F0.wireOp",EDGE,"E12"),sQuery(id+"F0.wireOp",EDGE,"E13"),sQuery(id+"F0.wireOp",EDGE,"E14"),sQuery(id+"F0.wireOp",EDGE,"E15"),sQuery(id+"F0.wireOp",EDGE,"E17.filletArc"),sQuery(id+"F0.wireOp",EDGE,"E18.filletArc"),sQuery(id+"F0.wireOp",EDGE,"E19.filletArc"),sQuery(id+"F0.wireOp",EDGE,"E20.filletArc"),sQuery(id+"F0.wireOp",EDGE,"E25.0"),sQuery(id+"F0.wireOp",EDGE,"E25.1"),sQuery(id+"F0.wireOp",EDGE,"E25.2"),sQuery(id+"F0.wireOp",EDGE,"E25.3"),sQuery(id+"F0.wireOp",EDGE,"E25.4"),sQuery(id+"F0.wireOp",EDGE,"E25.5"),sQuery(id+"F0.wireOp",EDGE,"E25.6"),sQuery(id+"F0.wireOp",EDGE,"E25.7")])],"isStart":false});
            extrude(context, id + "F17", {"entities" : qUnion([Q0, Q1, Q2]), "endBound" : BoundingType.UP_TO_SURFACE, "endBoundEntityFace" : qUnion([Q3]), "depth" : 25 * mm});
        }
    });
